# Revit family: Grohe_BasinMixer_Essence_24170KF1
name_source: partatom
category: Plumbing Fixtures
units: mm (PartAtom-declared; Revit-internal decimal feet)

## family parameters
Cut with Voids When Loaded = No
Host = Face
OmniClass Number = 23.45.05.00
OmniClass Title = Sanitary Equipment
Part Type = Normal
Room Calculation Point = No
Round Connector Dimension = Use Diameter
Shared = No

## types (1)
- ESSENCE Basin Mixer (24170KF1)
    Assembly Code = D2010
    AssetType = Fixed
    BIMObjectName = Grohe_BasinMixer_Essence_24170KF1
    CO2NeutralProduction = GROHE is one of the first leading manufacturer within the sanitary industry having a CO2-neutral production.
    CW Connection = Yes
    ClassificationName = Uniclass2015
    ClassificationValue = Pr_40_20_87_55
    Color = Matt Black
    Cost = 0 $
    Default Elevation = 0 mm  [stored 0 ft]
    Description = ESSENCE Basin Mixer
    DimensionsDocumentLink = https://cdn.cloud.grohe.com
    DocumentationCertificates = https://www.bimstore.co
    DocumentationInstallationGuide = https://www.bimstore.co
    DocumentationLiterature = https://www.bimstore.co
    DocumentationMaintenance = https://www.bimstore.co
    DocumentationTechnical = https://www.bimstore.co
    DurationUnit = Years
    EF000003 = Top/tap hole
    EF000139 = Other
    EF001707 = 70 °C
    EF002149 = TRUE
    EF002286 = Hose (gland nut)
    EF002671 = Black
    EF007955 = FALSE
    EF011775 = not applicable
    EF011779 = FALSE
    EF011781 = not applicable
    EF012753 = 6.5
    EF014578 = not applicable
    EF014591 = FALSE
    EF015280 = FALSE
    EF016731 = Group I,<= 20 dB(A)
    EF020075 = Yes
    EF020105 = No
    EF020780 = Single-grip
    EF020781 = Cartouche, ceramic
    EF020785 = 3/8 inch
    EF020787 = Group II, <=30 dB(A)
    EF020789 = 179 mm  [stored 0.58727 ft]
    EF020791 = Brass
    EF020792 = FALSE
    EF020794 = TRUE
    EF020795 = Fixed
    EF020796 = 364 mm  [stored 1.19423 ft]
    EF020797 = 322 mm  [stored 1.05643 ft]
    EF020798 = not relevant
    EF020799 = TRUE
    EF020801 = FALSE
    EF021808 = 1-hole
    EF021835 = 0 mm  [stored 0 ft]
    EF022042 = None
    EF022168 = FALSE
    EF022750 = Pipe
    EF023686 = not applicable
    EF023687 = FALSE
    EF023688 = Foam jet nozzle
    EF025109 = Other
    EFDE0046 = Group I, <=20 dB(A)
    EFSE0002 = TRUE
    Ecojoy = No
    ExpectedLife = 0
    FullRecyclabilityOfPlastic = All plastic components are fully recyclable
    GROHESocialCommittment = green.grohe.com/social_engagement
    GROHESustainability = green.grohe.com
    HW Connection = Yes
    IfcExportAs = IfcPipeFitting
    IfcExportType = IfcPipeFittingType
    Keynote = N13
    Manufacturer = Grohe
    ManufacturerName = Grohe
    Model = ESSENCE Basin Mixer
    ModelNumber = 24170KF1
    ModelReference = ESSENCE Basin Mixer
    NBSDescription = Mixer taps
    NBSObjectName = Grohe - Mixer taps
    NBSReference = 45-35-70/345
    NominalDepth = 0 mm  [stored 0 ft]
    NominalHeight = 0 mm  [stored 0 ft]
    NominalLength = 0 mm  [stored 0 ft]
    PQDiagramLink = https://cdn.cloud.grohe.com
    PrimaryMaterial = Grohe_MattBlack
    ProductDescription = single hole installation

metal lever

GROHE SilkMove 28 mm ceramic cartridge

with temperature limiter

GROHE Long-Life Shine finish

GROHE Water Saving mousseur 5.7 l/min

GROHE AquaGuide adjustable mousseur

GROHE FastFixation Plus installation system

swivel spout with mousseur and stop limiter

smooth body

flexible connection hoses

min. recommended pressure 1.0 bar
    ProductNumber = 24170KF1
    ProductPageURL = https://www.grohe.co.uk
    ProductShortText = Essence Basin mixer 1/2" XL-Size
    ProductType = Single Lever Mixer
    ProductionYear = 2023
    SustainabilityAward = green.grohe.com/awards
    SustainabilityReport = green.grohe.com/reporting
    TPIDocumentLink = https://cdn.cloud.grohe.com
    Type Comments = ESSENCE Basin Mixer
    TypeName = ESSENCE Basin Mixer
    URL = https://www.grohe.co.uk
    Vent Connection = No
    WarrantyDurationLabor = 0
    WarrantyDurationParts = 0
    WarrantyDurationUnit = Years
    Waste Connection = No
    _BSBibleVersion = 17
    _BimSpecGuid = 0
    _CurrentRevision = 1
    _DistributedBy = https://www.bimstore.co
    _ObjectUserGuide = https://www.bimstore.co

note: [stored X ft] marks values corroborated as IEEE doubles in the binary element streams (Revit-internal decimal feet)

## geometry (parser evidence)
native form markers: Sweep x2
no freeform markers — native parametric forms only
